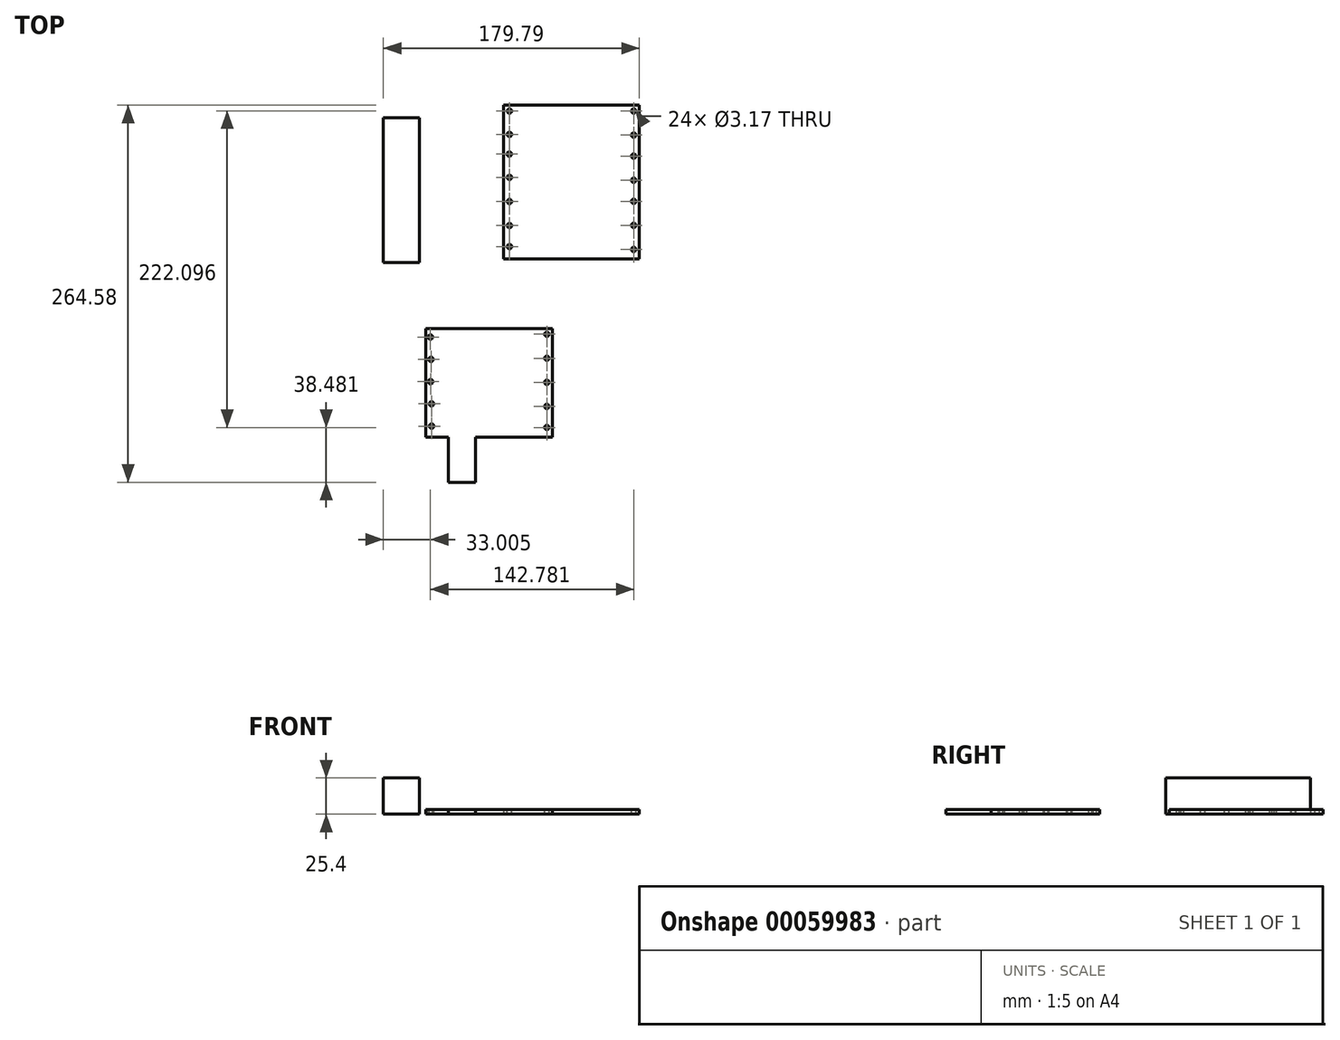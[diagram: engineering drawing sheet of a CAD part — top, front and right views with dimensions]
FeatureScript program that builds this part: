
annotation { "Feature Type Name" : "Feature", "Feature Type Description" : "" }
export const myFeature = defineFeature(function(context is Context, id is Id, definition is map)
    precondition{}
    {
        {
            var Q0;
            Q0=qCreatedBy(makeId("Top.planeOp"),FACE);
            var sketch = newSketch(context, id + "F0", { "sketchPlane" : qUnion([Q0])});
            skLineSegment(sketch, "E0.bottom", {"start": v(0, 0) * mm, "end": v(-88.9, 0) * mm});
            skLineSegment(sketch, "E0.top", {"start": v(0, -76.2) * mm, "end": v(-88.9, -76.2) * mm});
            skLineSegment(sketch, "E0.left", {"start": v(0, 0) * mm, "end": v(0, -76.2) * mm});
            skLineSegment(sketch, "E0.right", {"start": v(-88.9, 0) * mm, "end": v(-88.9, -76.2) * mm});
            skSolve(sketch);
        }
        {
            var Q0;
            Q0 = qSketchRegion(id + "F0", true);
            extrude(context, id + "F1", {"entities" : qUnion([Q0]), "depth" : 3.17 * mm});
        }
        {
            var Q0;
            Q0=qCreatedBy(makeId("Top.planeOp"),FACE);
            var sketch = newSketch(context, id + "F2", { "sketchPlane" : qUnion([Q0])});
            skLineSegment(sketch, "E1.bottom", {"start": v(61.02, 48.68) * mm, "end": v(-34.23, 48.68) * mm});
            skLineSegment(sketch, "E1.top", {"start": v(61.02, 156.63) * mm, "end": v(-34.23, 156.63) * mm});
            skLineSegment(sketch, "E1.left", {"start": v(61.02, 48.68) * mm, "end": v(61.02, 156.63) * mm});
            skLineSegment(sketch, "E1.right", {"start": v(-34.23, 48.68) * mm, "end": v(-34.23, 156.63) * mm});
            skSolve(sketch);
        }
        {
            var Q0;
            Q0 = qSketchRegion(id + "F2", true);
            extrude(context, id + "F3", {"entities" : qUnion([Q0]), "depth" : 3.17 * mm});
        }
        {
            var Q0;
            Q0=qCreatedBy(makeId("Top.planeOp"),FACE);
            var sketch = newSketch(context, id + "F4", { "sketchPlane" : qUnion([Q0])});
            skLineSegment(sketch, "E2.bottom", {"start": v(-118.77, 147.85) * mm, "end": v(-93.37, 147.85) * mm});
            skLineSegment(sketch, "E2.top", {"start": v(-118.77, 46.25) * mm, "end": v(-93.37, 46.25) * mm});
            skLineSegment(sketch, "E2.left", {"start": v(-118.77, 147.85) * mm, "end": v(-118.77, 46.25) * mm});
            skLineSegment(sketch, "E2.right", {"start": v(-93.37, 147.85) * mm, "end": v(-93.37, 46.25) * mm});
            skSolve(sketch);
        }
        {
            var Q0;
            Q0=makeQuery(id+"F4.imprint","IMPRINT",FACE,{"disambiguationData":[TD([[makeQuery(id+"F4.imprint","IMPRINT",EDGE,{"derivedFrom":sQuery(id+"F4.wireOp",EDGE,"E2.bottom")}),-1.0]])]});
            extrude(context, id + "F5", {"entities" : qUnion([Q0]), "depth" : 25.4 * mm});
        }
        {
            var Q0;
            Q0=makeQuery(id+"F3.opExtrude","CAP_FACE",FACE,{"disambiguationData":[OSD([sQuery(id+"F2.wireOp",EDGE,"E1.bottom"),sQuery(id+"F2.wireOp",EDGE,"E1.top"),sQuery(id+"F2.wireOp",EDGE,"E1.left"),sQuery(id+"F2.wireOp",EDGE,"E1.right")])],"isStart":false});
            var sketch = newSketch(context, id + "F6", { "sketchPlane" : qUnion([Q0])});
            skCircle(sketch, "E3", {"center": v(-30.23, 152.63) * mm, "radius": 2.1 * mm});
            skSolve(sketch);
        }
        {
            var Q0;
            Q0=sQuery(id+"F6.wireOp",VERTEX,"E3.center");
            var Q1;
            Q1=makeQuery(id+"F3.opExtrude","SWEPT_BODY",BODY,{"disambiguationData":[OSD([sQuery(id+"F2.wireOp",EDGE,"E1.bottom"),sQuery(id+"F2.wireOp",EDGE,"E1.top"),sQuery(id+"F2.wireOp",EDGE,"E1.left"),sQuery(id+"F2.wireOp",EDGE,"E1.right")])]});
            hole(context, id + "F7", {"style" : HoleStyle.SIMPLE, "holeDiameter" : 3.17 * mm, "endStyle" : HoleEndStyle.THROUGH, "locations" : qUnion([Q0]), "scope" : qUnion([Q1])});
        }
        {
            var Q0;
            Q0=makeQuery(id+"F3.opExtrude","CAP_FACE",FACE,{"disambiguationData":[OSD([sQuery(id+"F2.wireOp",EDGE,"E1.bottom"),sQuery(id+"F2.wireOp",EDGE,"E1.top"),sQuery(id+"F2.wireOp",EDGE,"E1.left"),sQuery(id+"F2.wireOp",EDGE,"E1.right")])],"isStart":false});
            var sketch = newSketch(context, id + "F8", { "sketchPlane" : qUnion([Q0])});
            skCircle(sketch, "E4", {"center": v(-30.23, 136.24) * mm, "radius": 2.1 * mm});
            skSolve(sketch);
        }
        {
            var Q0;
            Q0=sQuery(id+"F8.wireOp",VERTEX,"E4.center");
            var Q1;
            Q1=makeQuery(id+"F3.opExtrude","SWEPT_BODY",BODY,{"disambiguationData":[OSD([sQuery(id+"F2.wireOp",EDGE,"E1.bottom"),sQuery(id+"F2.wireOp",EDGE,"E1.top"),sQuery(id+"F2.wireOp",EDGE,"E1.left"),sQuery(id+"F2.wireOp",EDGE,"E1.right")])]});
            hole(context, id + "F9", {"style" : HoleStyle.SIMPLE, "holeDiameter" : 3.17 * mm, "endStyle" : HoleEndStyle.THROUGH, "locations" : qUnion([Q0]), "scope" : qUnion([Q1])});
        }
        {
            var Q0;
            Q0=makeQuery(id+"F3.opExtrude","CAP_FACE",FACE,{"disambiguationData":[OSD([sQuery(id+"F2.wireOp",EDGE,"E1.bottom"),sQuery(id+"F2.wireOp",EDGE,"E1.top"),sQuery(id+"F2.wireOp",EDGE,"E1.left"),sQuery(id+"F2.wireOp",EDGE,"E1.right")])],"isStart":false});
            var sketch = newSketch(context, id + "F10", { "sketchPlane" : qUnion([Q0])});
            skCircle(sketch, "E5", {"center": v(-30.3, 122.4) * mm, "radius": 2.1 * mm});
            skSolve(sketch);
        }
        {
            var Q0;
            Q0=sQuery(id+"F10.wireOp",VERTEX,"E5.center");
            var Q1;
            Q1=makeQuery(id+"F3.opExtrude","SWEPT_BODY",BODY,{"disambiguationData":[OSD([sQuery(id+"F2.wireOp",EDGE,"E1.bottom"),sQuery(id+"F2.wireOp",EDGE,"E1.top"),sQuery(id+"F2.wireOp",EDGE,"E1.left"),sQuery(id+"F2.wireOp",EDGE,"E1.right")])]});
            hole(context, id + "F11", {"style" : HoleStyle.SIMPLE, "holeDiameter" : 3.17 * mm, "endStyle" : HoleEndStyle.THROUGH, "locations" : qUnion([Q0]), "scope" : qUnion([Q1])});
        }
        {
            var Q0;
            Q0=makeQuery(id+"F3.opExtrude","CAP_FACE",FACE,{"disambiguationData":[OSD([sQuery(id+"F2.wireOp",EDGE,"E1.bottom"),sQuery(id+"F2.wireOp",EDGE,"E1.top"),sQuery(id+"F2.wireOp",EDGE,"E1.left"),sQuery(id+"F2.wireOp",EDGE,"E1.right")])],"isStart":false});
            var sketch = newSketch(context, id + "F12", { "sketchPlane" : qUnion([Q0])});
            skCircle(sketch, "E6", {"center": v(-30.23, 106.02) * mm, "radius": 2.1 * mm});
            skCircle(sketch, "E7", {"center": v(-30.23, 89.13) * mm, "radius": 2.1 * mm});
            skCircle(sketch, "E8", {"center": v(-30.23, 72.24) * mm, "radius": 2.1 * mm});
            skCircle(sketch, "E9", {"center": v(-30.23, 57.44) * mm, "radius": 2.1 * mm});
            skSolve(sketch);
        }
        {
            var Q0;
            Q0=sQuery(id+"F12.wireOp",VERTEX,"E6.center");
            var Q1;
            Q1=sQuery(id+"F12.wireOp",VERTEX,"E7.center");
            var Q2;
            Q2=sQuery(id+"F12.wireOp",VERTEX,"E8.center");
            var Q3;
            Q3=sQuery(id+"F12.wireOp",VERTEX,"E9.center");
            var Q4;
            Q4=makeQuery(id+"F3.opExtrude","SWEPT_BODY",BODY,{"disambiguationData":[OSD([sQuery(id+"F2.wireOp",EDGE,"E1.bottom"),sQuery(id+"F2.wireOp",EDGE,"E1.top"),sQuery(id+"F2.wireOp",EDGE,"E1.left"),sQuery(id+"F2.wireOp",EDGE,"E1.right")])]});
            hole(context, id + "F13", {"style" : HoleStyle.SIMPLE, "holeDiameter" : 3.17 * mm, "endStyle" : HoleEndStyle.THROUGH, "locations" : qUnion([Q0, Q1, Q2, Q3]), "scope" : qUnion([Q4])});
        }
        {
            var Q0;
            Q0=makeQuery(id+"F3.opExtrude","CAP_FACE",FACE,{"disambiguationData":[OSD([sQuery(id+"F2.wireOp",EDGE,"E1.bottom"),sQuery(id+"F2.wireOp",EDGE,"E1.top"),sQuery(id+"F2.wireOp",EDGE,"E1.left"),sQuery(id+"F2.wireOp",EDGE,"E1.right")])],"isStart":false});
            var sketch = newSketch(context, id + "F14", { "sketchPlane" : qUnion([Q0])});
            skCircle(sketch, "E10", {"center": v(57.02, 152.63) * mm, "radius": 2.1 * mm});
            skCircle(sketch, "E11", {"center": v(57.02, 135.74) * mm, "radius": 2.1 * mm});
            skCircle(sketch, "E12", {"center": v(57.02, 120.94) * mm, "radius": 2.1 * mm});
            skCircle(sketch, "E13", {"center": v(57.02, 104.05) * mm, "radius": 2.1 * mm});
            skCircle(sketch, "E14", {"center": v(56.95, 89.25) * mm, "radius": 2.1 * mm});
            skCircle(sketch, "E15", {"center": v(57.02, 72.36) * mm, "radius": 2.1 * mm});
            skCircle(sketch, "E16", {"center": v(57.02, 55.47) * mm, "radius": 2.1 * mm});
            skSolve(sketch);
        }
        {
            var Q0;
            Q0=sQuery(id+"F14.wireOp",VERTEX,"E10.center");
            var Q1;
            Q1=sQuery(id+"F14.wireOp",VERTEX,"E11.center");
            var Q2;
            Q2=sQuery(id+"F14.wireOp",VERTEX,"E12.center");
            var Q3;
            Q3=sQuery(id+"F14.wireOp",VERTEX,"E13.center");
            var Q4;
            Q4=sQuery(id+"F14.wireOp",VERTEX,"E14.center");
            var Q5;
            Q5=sQuery(id+"F14.wireOp",VERTEX,"E15.center");
            var Q6;
            Q6=sQuery(id+"F14.wireOp",VERTEX,"E16.center");
            var Q7;
            Q7=makeQuery(id+"F3.opExtrude","SWEPT_BODY",BODY,{"disambiguationData":[OSD([sQuery(id+"F2.wireOp",EDGE,"E1.bottom"),sQuery(id+"F2.wireOp",EDGE,"E1.top"),sQuery(id+"F2.wireOp",EDGE,"E1.left"),sQuery(id+"F2.wireOp",EDGE,"E1.right")])]});
            hole(context, id + "F15", {"style" : HoleStyle.SIMPLE, "holeDiameter" : 3.17 * mm, "endStyle" : HoleEndStyle.THROUGH, "locations" : qUnion([Q0, Q1, Q2, Q3, Q4, Q5, Q6]), "scope" : qUnion([Q7])});
        }
        {
            var Q0;
            Q0=makeQuery(id+"F1.opExtrude","CAP_FACE",FACE,{"disambiguationData":[OSD([sQuery(id+"F0.wireOp",EDGE,"E0.bottom"),sQuery(id+"F0.wireOp",EDGE,"E0.top"),sQuery(id+"F0.wireOp",EDGE,"E0.left"),sQuery(id+"F0.wireOp",EDGE,"E0.right")])],"isStart":false});
            var sketch = newSketch(context, id + "F16", { "sketchPlane" : qUnion([Q0])});
            skCircle(sketch, "E17", {"center": v(-85.76, -6.04) * mm, "radius": 2.1 * mm});
            skCircle(sketch, "E18", {"center": v(-85.3, -21.65) * mm, "radius": 2.1 * mm});
            skCircle(sketch, "E19", {"center": v(-85.55, -37.27) * mm, "radius": 2.1 * mm});
            skCircle(sketch, "E20", {"center": v(-84.9, -52.88) * mm, "radius": 2.1 * mm});
            skCircle(sketch, "E21", {"center": v(-84.9, -68.5) * mm, "radius": 2.1 * mm});
            skSolve(sketch);
        }
        {
            var Q0;
            Q0=sQuery(id+"F16.wireOp",VERTEX,"E17.center");
            var Q1;
            Q1=sQuery(id+"F16.wireOp",VERTEX,"E18.center");
            var Q2;
            Q2=sQuery(id+"F16.wireOp",VERTEX,"E19.center");
            var Q3;
            Q3=sQuery(id+"F16.wireOp",VERTEX,"E20.center");
            var Q4;
            Q4=sQuery(id+"F16.wireOp",VERTEX,"E21.center");
            var Q5;
            Q5=makeQuery(id+"F1.opExtrude","SWEPT_BODY",BODY,{"disambiguationData":[OSD([sQuery(id+"F0.wireOp",EDGE,"E0.bottom"),sQuery(id+"F0.wireOp",EDGE,"E0.top"),sQuery(id+"F0.wireOp",EDGE,"E0.left"),sQuery(id+"F0.wireOp",EDGE,"E0.right")])]});
            hole(context, id + "F17", {"style" : HoleStyle.SIMPLE, "holeDiameter" : 3.17 * mm, "endStyle" : HoleEndStyle.THROUGH, "locations" : qUnion([Q0, Q1, Q2, Q3, Q4]), "scope" : qUnion([Q5])});
        }
        {
            var Q0;
            Q0=makeQuery(id+"F1.opExtrude","CAP_FACE",FACE,{"disambiguationData":[OSD([sQuery(id+"F0.wireOp",EDGE,"E0.bottom"),sQuery(id+"F0.wireOp",EDGE,"E0.top"),sQuery(id+"F0.wireOp",EDGE,"E0.left"),sQuery(id+"F0.wireOp",EDGE,"E0.right")])],"isStart":false});
            var sketch = newSketch(context, id + "F18", { "sketchPlane" : qUnion([Q0])});
            skCircle(sketch, "E22", {"center": v(-4, -4) * mm, "radius": 2.1 * mm});
            skCircle(sketch, "E23", {"center": v(-4, -20.9) * mm, "radius": 2.1 * mm});
            skCircle(sketch, "E24", {"center": v(-4, -37.78) * mm, "radius": 2.1 * mm});
            skCircle(sketch, "E25", {"center": v(-4, -54.67) * mm, "radius": 2.1 * mm});
            skCircle(sketch, "E26", {"center": v(-4, -69.47) * mm, "radius": 2.1 * mm});
            skSolve(sketch);
        }
        {
            var Q0;
            Q0=sQuery(id+"F18.wireOp",VERTEX,"E22.center");
            var Q1;
            Q1=sQuery(id+"F18.wireOp",VERTEX,"E23.center");
            var Q2;
            Q2=sQuery(id+"F18.wireOp",VERTEX,"E24.center");
            var Q3;
            Q3=sQuery(id+"F18.wireOp",VERTEX,"E25.center");
            var Q4;
            Q4=sQuery(id+"F18.wireOp",VERTEX,"E26.center");
            var Q5;
            Q5=makeQuery(id+"F1.opExtrude","SWEPT_BODY",BODY,{"disambiguationData":[OSD([sQuery(id+"F0.wireOp",EDGE,"E0.bottom"),sQuery(id+"F0.wireOp",EDGE,"E0.top"),sQuery(id+"F0.wireOp",EDGE,"E0.left"),sQuery(id+"F0.wireOp",EDGE,"E0.right")])]});
            hole(context, id + "F19", {"style" : HoleStyle.SIMPLE, "holeDiameter" : 3.17 * mm, "endStyle" : HoleEndStyle.THROUGH, "locations" : qUnion([Q0, Q1, Q2, Q3, Q4]), "scope" : qUnion([Q5])});
        }
        {
            var Q0;
            Q0=makeQuery(id+"F1.opExtrude","SWEPT_FACE",FACE,{"disambiguationData":[OSD([sQuery(id+"F0.wireOp",EDGE,"E0.top")])]});
            var sketch = newSketch(context, id + "F20", { "sketchPlane" : qUnion([Q0])});
            skLineSegment(sketch, "E27.bottom", {"start": v(-73.03, 3.18) * mm, "end": v(-53.98, 3.18) * mm});
            skLineSegment(sketch, "E27.top", {"start": v(-73.03, 0) * mm, "end": v(-53.98, 0) * mm});
            skLineSegment(sketch, "E27.left", {"start": v(-73.03, 3.18) * mm, "end": v(-73.03, 0) * mm});
            skLineSegment(sketch, "E27.right", {"start": v(-53.98, 3.18) * mm, "end": v(-53.98, 0) * mm});
            skSolve(sketch);
        }
        {
            var Q0;
            Q0=makeQuery(id+"F20.imprint","IMPRINT",FACE,{"disambiguationData":[TD([[makeQuery(id+"F20.imprint","IMPRINT",EDGE,{"derivedFrom":sQuery(id+"F20.wireOp",EDGE,"E27.bottom")}),1.0]])]});
            extrude(context, id + "F21", {"entities" : qUnion([Q0]), "operationType" : NewBodyOperationType.ADD, "depth" : 31.75 * mm});
        }
    });
